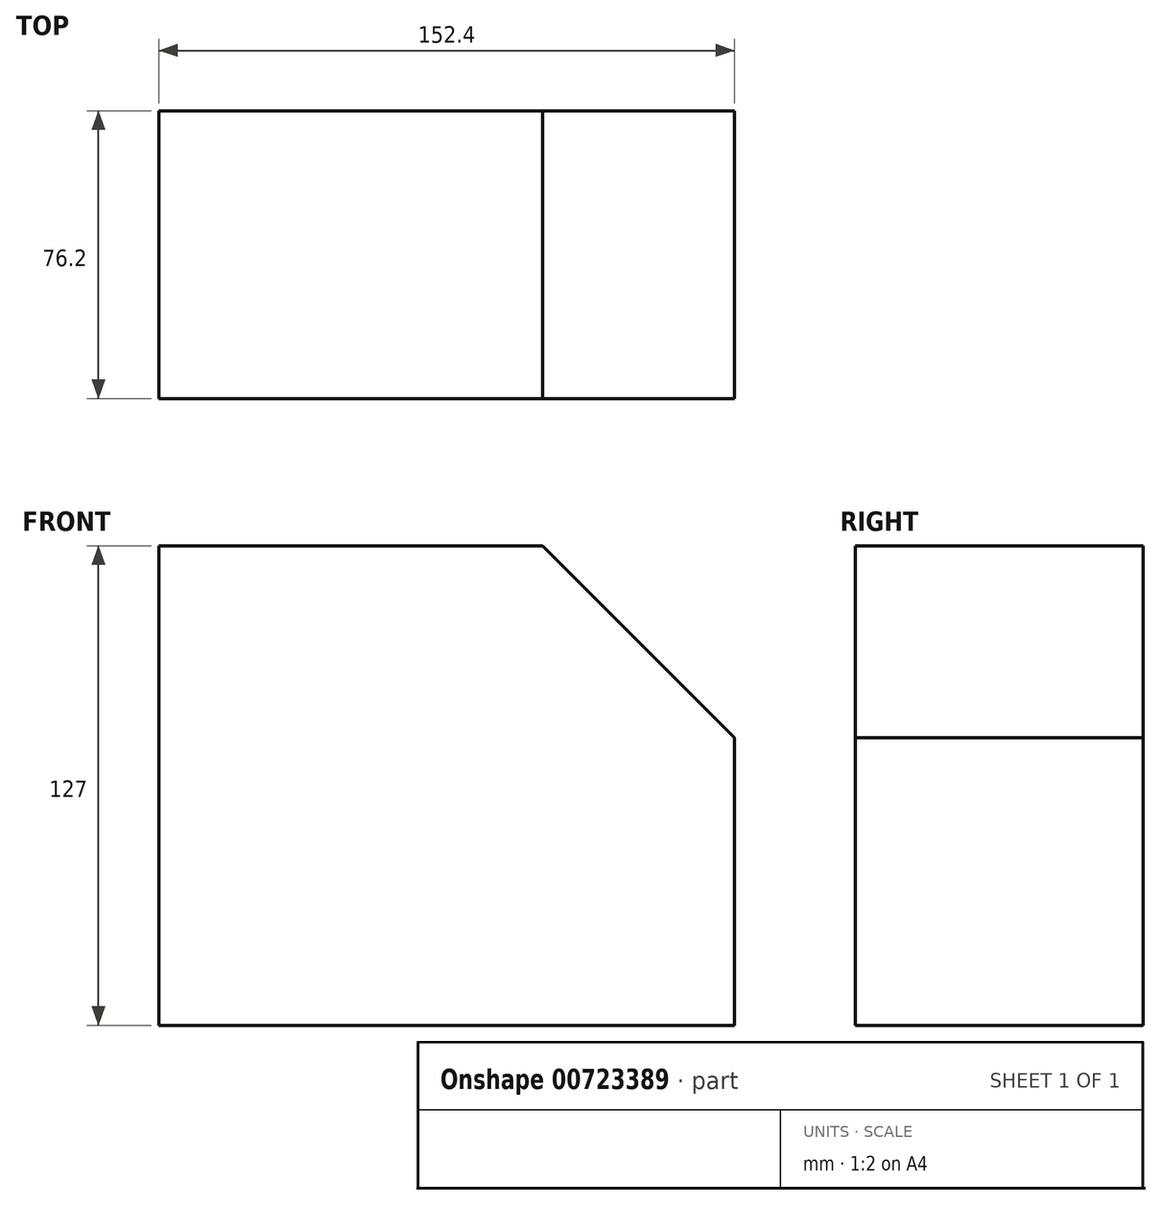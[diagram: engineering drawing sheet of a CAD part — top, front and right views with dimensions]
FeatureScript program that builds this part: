
annotation { "Feature Type Name" : "Feature", "Feature Type Description" : "" }
export const myFeature = defineFeature(function(context is Context, id is Id, definition is map)
    precondition{}
    {
        {
            var Q0;
            Q0=qCreatedBy(makeId("Front.planeOp"),FACE);
            var sketch = newSketch(context, id + "F0", { "sketchPlane" : qUnion([Q0])});
            skLineSegment(sketch, "E0", {"start": v(-55.04, -30.8) * mm, "end": v(-55.04, 96.2) * mm});
            skLineSegment(sketch, "E1", {"start": v(-55.04, 96.2) * mm, "end": v(46.56, 96.2) * mm});
            skLineSegment(sketch, "E2", {"start": v(-55.04, -30.8) * mm, "end": v(97.36, -30.8) * mm});
            skLineSegment(sketch, "E3", {"start": v(97.36, -30.8) * mm, "end": v(97.36, 45.4) * mm});
            skLineSegment(sketch, "E4", {"start": v(97.36, 45.4) * mm, "end": v(46.56, 96.2) * mm});
            skSolve(sketch);
        }
        {
            var Q0;
            Q0=makeQuery(id+"F0.imprint","IMPRINT",FACE,{"disambiguationData":[TD([[makeQuery(id+"F0.imprint","IMPRINT",EDGE,{"derivedFrom":sQuery(id+"F0.wireOp",EDGE,"E0")}),-1.0]])]});
            extrude(context, id + "F1", {"entities" : qUnion([Q0]), "depth" : 76.2 * mm, "offsetDistance" : 25.4 * mm});
        }
    });
